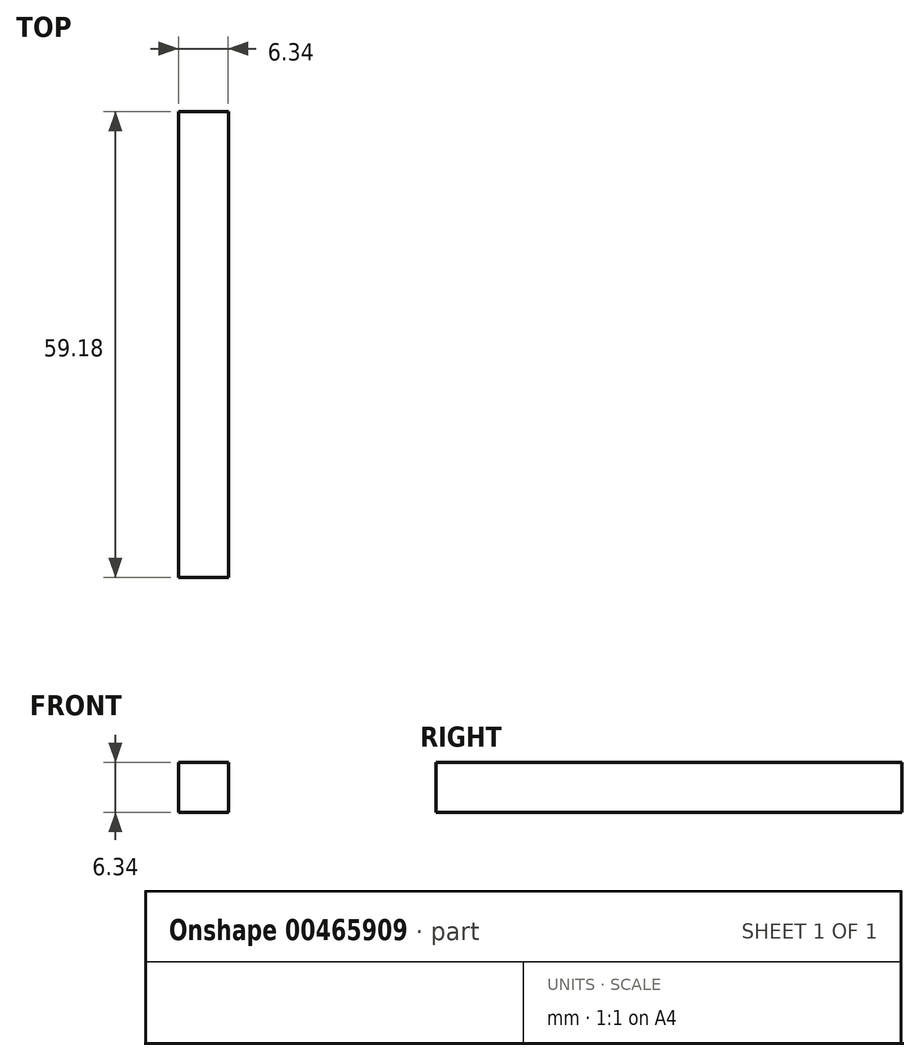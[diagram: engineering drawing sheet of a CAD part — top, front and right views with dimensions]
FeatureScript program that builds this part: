
annotation { "Feature Type Name" : "Feature", "Feature Type Description" : "" }
export const myFeature = defineFeature(function(context is Context, id is Id, definition is map)
    precondition{}
    {
        {
            var Q0;
            Q0=qCreatedBy(makeId("Front.planeOp"),FACE);
            var sketch = newSketch(context, id + "F0", { "sketchPlane" : qUnion([Q0])});
            skLineSegment(sketch, "E0.bottom", {"start": v(-3.18, 3.18) * mm, "end": v(3.18, 3.18) * mm});
            skLineSegment(sketch, "E0.top", {"start": v(-3.18, -3.18) * mm, "end": v(3.17, -3.18) * mm});
            skLineSegment(sketch, "E0.left", {"start": v(-3.17, 3.18) * mm, "end": v(-3.18, -3.18) * mm});
            skLineSegment(sketch, "E0.right", {"start": v(3.18, 3.18) * mm, "end": v(3.17, -3.18) * mm});
            skPoint(sketch, "E0.middle", {"position": v(0, 0) * mm});
            skSolve(sketch);
        }
        {
            var Q0;
            Q0=makeQuery(id+"F0.imprint","IMPRINT",FACE,{"disambiguationData":[TD([[makeQuery(id+"F0.imprint","IMPRINT",EDGE,{"derivedFrom":sQuery(id+"F0.wireOp",EDGE,"E0.bottom")}),-1.0]])]});
            extrude(context, id + "F1", {"entities" : qUnion([Q0]), "depth" : 59.18 * mm});
        }
    });
